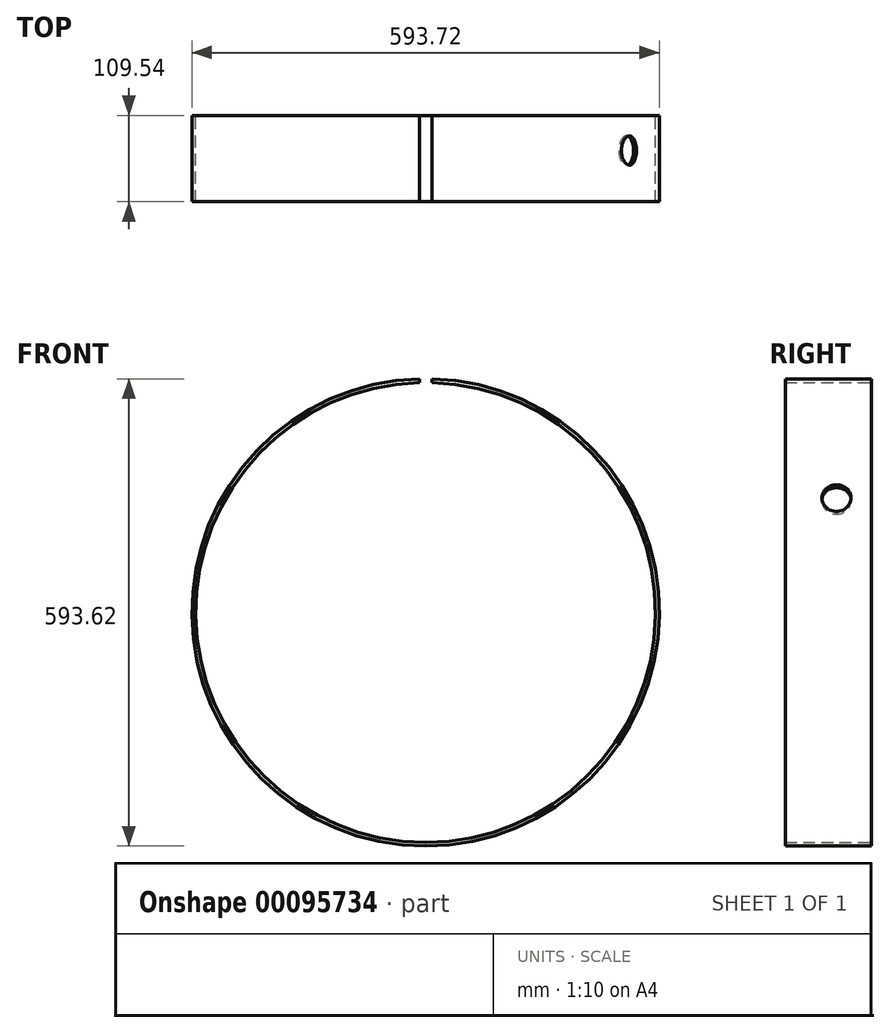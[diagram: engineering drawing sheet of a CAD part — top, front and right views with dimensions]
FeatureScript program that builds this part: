
annotation { "Feature Type Name" : "Feature", "Feature Type Description" : "" }
export const myFeature = defineFeature(function(context is Context, id is Id, definition is map)
    precondition{}
    {
        {
            var Q0;
            Q0=qCreatedBy(makeId("Front.planeOp"),FACE);
            var sketch = newSketch(context, id + "F0", { "sketchPlane" : qUnion([Q0])});
            skCircle(sketch, "E0", {"center": v(0, 0) * mm, "radius": 292.1 * mm});
            skCircle(sketch, "E1", {"center": v(0, 0) * mm, "radius": 296.86 * mm});
            skSolve(sketch);
        }
        {
            var Q0;
            Q0 = qSketchRegion(id + "F0", true);
            extrude(context, id + "F1", {"entities" : qUnion([Q0]), "depth" : 109.54 * mm});
        }
        {
            var Q0;
            Q0=qCreatedBy(makeId("Top.planeOp"),FACE);
            var sketch = newSketch(context, id + "F2", { "sketchPlane" : qUnion([Q0])});
            skLineSegment(sketch, "E2.bottom", {"start": v(7.85, -121.71) * mm, "end": v(-7.85, -121.71) * mm});
            skLineSegment(sketch, "E2.top", {"start": v(7.85, 121.71) * mm, "end": v(-7.85, 121.71) * mm});
            skLineSegment(sketch, "E2.left", {"start": v(7.85, -121.71) * mm, "end": v(7.85, 121.71) * mm});
            skLineSegment(sketch, "E2.right", {"start": v(-7.85, -121.71) * mm, "end": v(-7.85, 121.71) * mm});
            skPoint(sketch, "E2.middle", {"position": v(0, 0) * mm});
            skSolve(sketch);
        }
        {
            var Q0;
            Q0 = qSketchRegion(id + "F2", true);
            extrude(context, id + "F3", {"entities" : qUnion([Q0]), "operationType" : NewBodyOperationType.REMOVE, "depth" : 304.8 * mm});
        }
        {
            var Q0;
            Q0=qCreatedBy(makeId("Right.planeOp"),FACE);
            var Q1;
            Q1=qCreatedBy(makeId("Top.planeOp"),FACE);
            cPlane(context, id + "F4", {"entities" : qUnion([Q0, Q1]), "cplaneType" : CPlaneType.MID_PLANE, "offset" : 152.4 * mm, "flipAlignment" : true, "width" : 152.4 * mm, "height" : 152.4 * mm});
        }
        {
            var Q0;
            Q0=qCreatedBy(id+"F4.planeOp",FACE);
            var sketch = newSketch(context, id + "F5", { "sketchPlane" : qUnion([Q0])});
            skCircle(sketch, "E3", {"center": v(-44.45, -80) * mm, "radius": 18.56 * mm});
            skSolve(sketch);
        }
        {
            var Q0;
            Q0 = qSketchRegion(id + "F5", true);
            extrude(context, id + "F6", {"entities" : qUnion([Q0]), "operationType" : NewBodyOperationType.REMOVE, "depth" : 304.8 * mm});
        }
    });
